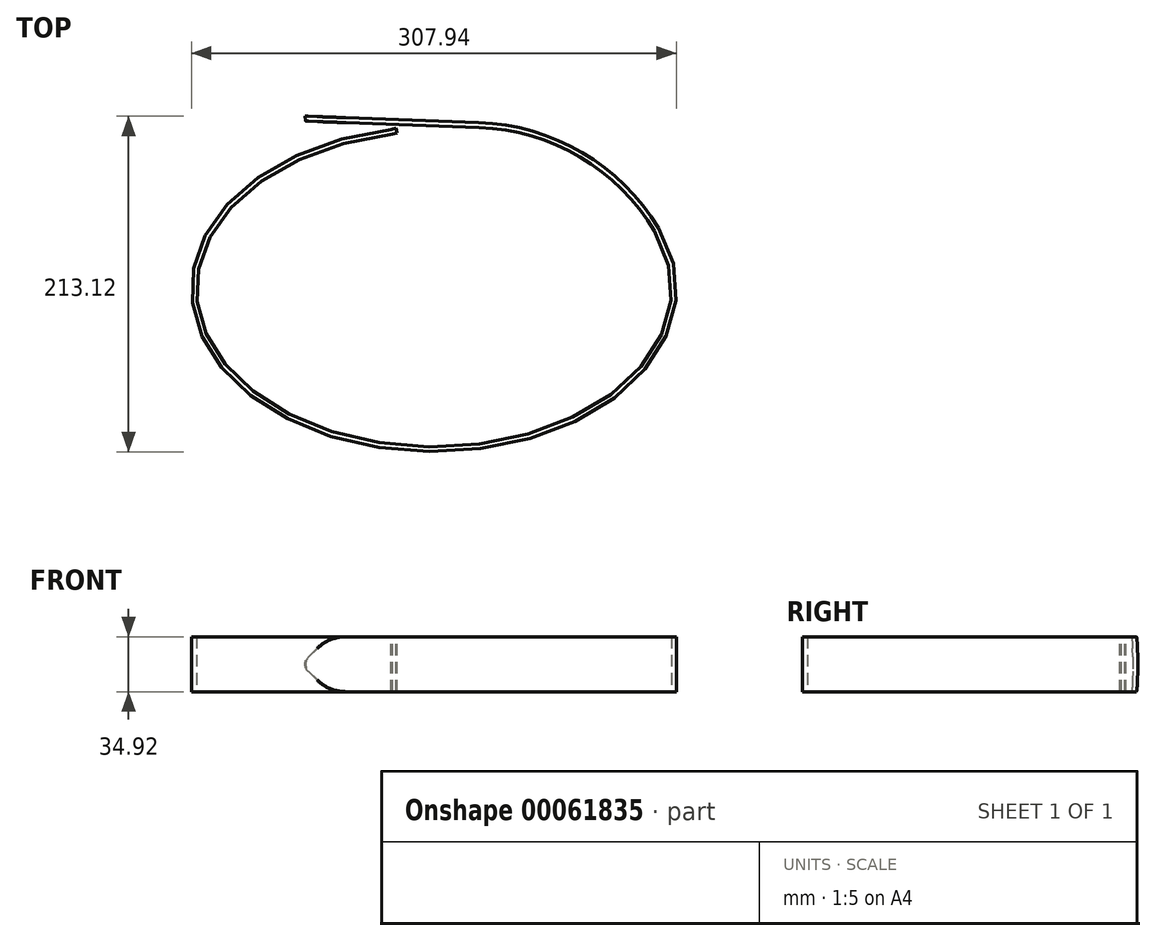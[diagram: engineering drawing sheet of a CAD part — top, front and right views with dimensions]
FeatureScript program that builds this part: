
annotation { "Feature Type Name" : "Feature", "Feature Type Description" : "" }
export const myFeature = defineFeature(function(context is Context, id is Id, definition is map)
    precondition{}
    {
        {
            var Q0;
            Q0=qCreatedBy(makeId("Top.planeOp"),FACE);
            var sketch = newSketch(context, id + "F0", { "sketchPlane" : qUnion([Q0])});
            skEllipticalArc(sketch, "E0", {});
            skLineSegment(sketch, "E1", {"start": v(0, 0) * mm, "end": v(-29.72, 110.93) * mm, "construction": true});
            skLineSegment(sketch, "E2", {"start": v(0, 0) * mm, "end": v(108.12, 28.97) * mm, "construction": true});
            skLineSegment(sketch, "E3", {"start": v(141.4, 37.89) * mm, "end": v(141.4, 37.89) * mm});
            skArc(sketch, "E4", {"start": v(141.4, 37.89) * mm, "mid": v(93.41, 85.4) * mm, "end": v(28.6, 104.35) * mm});
            skLineSegment(sketch, "E5", {"start": v(28.6, 104.35) * mm, "end": v(-92.38, 108.76) * mm});
            const initialGuessF0  = {"E0": [0, 0, -1, 0, 0.1524, 0.1016, 4.889157305840417, 3.5237563682352877]};
            skSetInitialGuess(sketch, initialGuessF0);
            skSolve(sketch);
        }
        {
            var Q0;
            Q0=qCreatedBy(makeId("Right.planeOp"),FACE);
            var Q1;
            Q1=sQuery(id+"F0.wireOp",EDGE,"E1");
            cPlane(context, id + "F1", {"entities" : qUnion([Q0, Q1]), "cplaneType" : CPlaneType.LINE_ANGLE, "offset" : 152.4 * mm, "angle" : 0 * degree, "width" : 152.4 * mm, "height" : 152.4 * mm});
        }
        {
            var Q0;
            Q0=qCreatedBy(id+"F1.planeOp",FACE);
            var sketch = newSketch(context, id + "F2", { "sketchPlane" : qUnion([Q0])});
            skLineSegment(sketch, "E6.rect.bottom", {"start": v(-105.13, -17.46) * mm, "end": v(-101.96, -17.46) * mm});
            skLineSegment(sketch, "E6.rect.top", {"start": v(-105.13, 17.46) * mm, "end": v(-101.96, 17.46) * mm});
            skLineSegment(sketch, "E6.rect.left", {"start": v(-105.13, -17.46) * mm, "end": v(-105.13, 17.46) * mm});
            skLineSegment(sketch, "E6.rect.right", {"start": v(-101.96, -17.46) * mm, "end": v(-101.96, 17.46) * mm});
            skPoint(sketch, "E6.rect.middle", {"position": v(-103.54, 0) * mm});
            skSolve(sketch);
        }
        {
            var Q0;
            Q0=makeQuery(id+"F2.imprint","IMPRINT",FACE,{"disambiguationData":[TD([[makeQuery(id+"F2.imprint","IMPRINT",EDGE,{"derivedFrom":sQuery(id+"F2.wireOp",EDGE,"E6.rect.bottom")}),1.0]])]});
            var Q1;
            Q1=sQuery(id+"F0.wireOp",EDGE,"E0");
            var Q2;
            Q2=sQuery(id+"F0.wireOp",EDGE,"E4");
            var Q3;
            Q3=sQuery(id+"F0.wireOp",EDGE,"E5");
            sweep(context, id + "F3", {"profiles" : qUnion([Q0]), "path" : qUnion([Q1, Q2, Q3])});
        }
        {
            var Q0;
            Q0=makeQuery(id+"F3.opSweep","CAP_FACE",FACE,{"disambiguationData":[OSD([sQuery(id+"F0.wireOp",VERTEX,"E0.start"),sQuery(id+"F2.wireOp",EDGE,"E6.rect.bottom"),sQuery(id+"F2.wireOp",EDGE,"E6.rect.top"),sQuery(id+"F2.wireOp",EDGE,"E6.rect.left"),sQuery(id+"F2.wireOp",EDGE,"E6.rect.right")])],"isStart":true});
            var sketch = newSketch(context, id + "F4", { "sketchPlane" : qUnion([Q0])});
            skLineSegment(sketch, "E7.0.0", {"start": v(105.13, 17.46) * mm, "end": v(105.13, -17.46) * mm});
            skLineSegment(sketch, "E7.0.1", {"start": v(101.96, 17.46) * mm, "end": v(105.13, 17.46) * mm});
            skLineSegment(sketch, "E7.0.2", {"start": v(101.96, 17.46) * mm, "end": v(101.96, -17.46) * mm});
            skLineSegment(sketch, "E7.0.3", {"start": v(101.96, -17.46) * mm, "end": v(105.13, -17.46) * mm});
            skSolve(sketch);
        }
        {
            var Q0;
            Q0 = qSketchRegion(id + "F4", true);
            extrude(context, id + "F5", {"entities" : qUnion([Q0]), "operationType" : NewBodyOperationType.ADD, "depth" : 3.17 * mm});
        }
        {
            var Q0;
            Q0=makeQuery(id+"F3.opSweep","CAP_EDGE",EDGE,{"disambiguationData":[OSD([sQuery(id+"F0.wireOp",VERTEX,"E5.end"),sQuery(id+"F2.wireOp",EDGE,"E6.rect.top")])],"isStart":false});
            var Q1;
            Q1=makeQuery(id+"F3.opSweep","CAP_EDGE",EDGE,{"disambiguationData":[OSD([sQuery(id+"F0.wireOp",VERTEX,"E5.end"),sQuery(id+"F2.wireOp",EDGE,"E6.rect.bottom")])],"isStart":false});
            chamfer(context, id + "F6", {"entities" : qUnion([Q0, Q1]), "width" : 25.4 * mm, "tangentPropagation" : true});
        }
        {
            var Q0;
            {var subQ0=sQuery(id+"F2.wireOp",EDGE,"E6.rect.top");Q0=makeQuery(id+"F6.opChamfer","BLEND_EDGE",EDGE,{"blendedFrom":[makeQuery(id+"F3.opSweep","CAP_EDGE",EDGE,{"disambiguationData":[OSD([sQuery(id+"F0.wireOp",VERTEX,"E5.end"),subQ0])],"isStart":false}),makeQuery(id+"F5.boolean.opBoolean","MERGE",FACE,{"derivedFrom":[makeQuery(id+"F3.opSweep","SWEPT_FACE",FACE,{"disambiguationData":[OSD([sQuery(id+"F0.wireOp",EDGE,"E0"),subQ0])]}),makeQuery(id+"F5.opExtrude","SWEPT_FACE",FACE,{"disambiguationData":[OSD([sQuery(id+"F4.wireOp",EDGE,"E7.0.1")])]})]})],"blendedInto":[makeQuery(id+"F5.boolean.opBoolean","MERGE",FACE,{"derivedFrom":[makeQuery(id+"F3.opSweep","SWEPT_FACE",FACE,{"disambiguationData":[OSD([sQuery(id+"F0.wireOp",EDGE,"E0"),subQ0])]}),makeQuery(id+"F5.opExtrude","SWEPT_FACE",FACE,{"disambiguationData":[OSD([sQuery(id+"F4.wireOp",EDGE,"E7.0.1")])]})]})]});}
            var Q1;
            {var subQ0=sQuery(id+"F2.wireOp",EDGE,"E6.rect.bottom");Q1=makeQuery(id+"F6.opChamfer","BLEND_EDGE",EDGE,{"blendedFrom":[makeQuery(id+"F3.opSweep","CAP_EDGE",EDGE,{"disambiguationData":[OSD([sQuery(id+"F0.wireOp",VERTEX,"E5.end"),subQ0])],"isStart":false}),makeQuery(id+"F5.boolean.opBoolean","MERGE",FACE,{"derivedFrom":[makeQuery(id+"F3.opSweep","SWEPT_FACE",FACE,{"disambiguationData":[OSD([sQuery(id+"F0.wireOp",EDGE,"E0"),subQ0])]}),makeQuery(id+"F5.opExtrude","SWEPT_FACE",FACE,{"disambiguationData":[OSD([sQuery(id+"F4.wireOp",EDGE,"E7.0.3")])]})]})],"blendedInto":[makeQuery(id+"F5.boolean.opBoolean","MERGE",FACE,{"derivedFrom":[makeQuery(id+"F3.opSweep","SWEPT_FACE",FACE,{"disambiguationData":[OSD([sQuery(id+"F0.wireOp",EDGE,"E0"),subQ0])]}),makeQuery(id+"F5.opExtrude","SWEPT_FACE",FACE,{"disambiguationData":[OSD([sQuery(id+"F4.wireOp",EDGE,"E7.0.3")])]})]})]});}
            fillet(context, id + "F7", {"entities" : qUnion([Q0, Q1]), "radius" : 25.4 * mm, "tangentPropagation" : true, "allowEdgeOverflow" : false});
        }
        {
            var Q0;
            {var subQ0=sQuery(id+"F0.wireOp",VERTEX,"E5.end");Q0=makeQuery(id+"F6.opChamfer","BLEND_EDGE",EDGE,{"blendedFrom":[makeQuery(id+"F3.opSweep","CAP_EDGE",EDGE,{"disambiguationData":[OSD([subQ0,sQuery(id+"F2.wireOp",EDGE,"E6.rect.bottom")])],"isStart":false}),makeQuery(id+"F3.opSweep","CAP_EDGE",EDGE,{"disambiguationData":[OSD([subQ0,sQuery(id+"F2.wireOp",EDGE,"E6.rect.top")])],"isStart":false})],"blendedInto":[]});}
            fillet(context, id + "F8", {"entities" : qUnion([Q0]), "radius" : 6.35 * mm, "tangentPropagation" : true, "allowEdgeOverflow" : false});
        }
        {
            var Q0;
            Q0=makeQuery(id+"F5.boolean.opBoolean","MERGE",FACE,{"derivedFrom":[makeQuery(id+"F3.opSweep","SWEPT_FACE",FACE,{"disambiguationData":[OSD([sQuery(id+"F0.wireOp",EDGE,"E0"),sQuery(id+"F2.wireOp",EDGE,"E6.rect.top")])]}),makeQuery(id+"F5.opExtrude","SWEPT_FACE",FACE,{"disambiguationData":[OSD([sQuery(id+"F4.wireOp",EDGE,"E7.0.1")])]})]});
            cPlane(context, id + "F9", {"entities" : qUnion([Q0]), "cplaneType" : CPlaneType.OFFSET, "offset" : 6.35 * mm, "width" : 152.4 * mm, "height" : 152.4 * mm});
        }
    });
